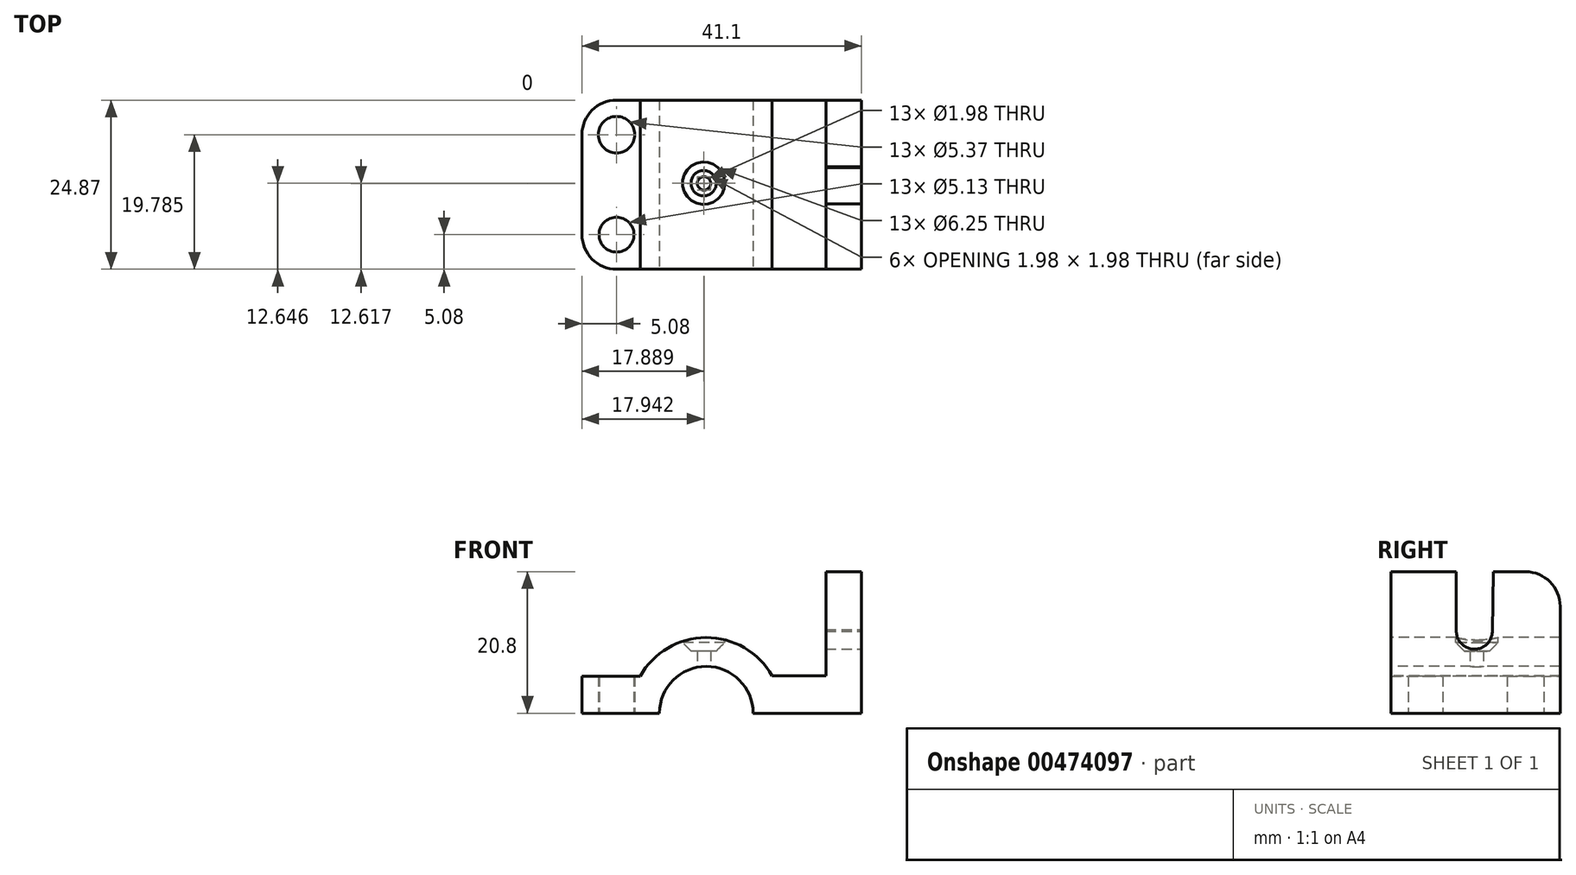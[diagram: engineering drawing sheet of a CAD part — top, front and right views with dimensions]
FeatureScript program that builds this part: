
annotation { "Feature Type Name" : "Feature", "Feature Type Description" : "" }
export const myFeature = defineFeature(function(context is Context, id is Id, definition is map)
    precondition{}
    {
        {
            var Q0;
            Q0=qCreatedBy(makeId("Top.planeOp"),FACE);
            var sketch = newSketch(context, id + "F0", { "sketchPlane" : qUnion([Q0])});
            skLineSegment(sketch, "E0.bottom", {"start": v(0, 0) * mm, "end": v(41.1, 0) * mm});
            skLineSegment(sketch, "E0.top", {"start": v(0, 24.87) * mm, "end": v(41.1, 24.87) * mm});
            skLineSegment(sketch, "E0.left", {"start": v(0, 0) * mm, "end": v(0, 24.87) * mm});
            skLineSegment(sketch, "E0.right", {"start": v(41.1, 0) * mm, "end": v(41.1, 24.87) * mm});
            skSolve(sketch);
        }
        {
            var Q0;
            Q0 = qSketchRegion(id + "F0", true);
            extrude(context, id + "F1", {"entities" : qUnion([Q0]), "depth" : 26.92 * mm});
        }
        {
            var Q0;
            Q0=qCreatedBy(makeId("Front.planeOp"),FACE);
            var sketch = newSketch(context, id + "F2", { "sketchPlane" : qUnion([Q0])});
            skArc(sketch, "E1", {"start": v(25.16, 0) * mm, "mid": v(18.28, 6.88) * mm, "end": v(11.4, 0) * mm});
            skArc(sketch, "E2", {"start": v(27.96, 5.5) * mm, "mid": v(18.23, 11.13) * mm, "end": v(8.55, 5.42) * mm});
            skLineSegment(sketch, "E3", {"start": v(0, 5.42) * mm, "end": v(8.55, 5.42) * mm});
            skLineSegment(sketch, "E4", {"start": v(27.96, 5.5) * mm, "end": v(35.86, 5.5) * mm});
            skLineSegment(sketch, "E5", {"start": v(35.86, 5.5) * mm, "end": v(35.86, 20.8) * mm});
            skLineSegment(sketch, "E6", {"start": v(35.86, 20.8) * mm, "end": v(43.18, 20.8) * mm});
            skLineSegment(sketch, "E7", {"start": v(43.18, 20.8) * mm, "end": v(42.24, 32.74) * mm});
            skLineSegment(sketch, "E8", {"start": v(42.24, 32.74) * mm, "end": v(-4.64, 32.74) * mm});
            skLineSegment(sketch, "E9", {"start": v(-4.64, 32.74) * mm, "end": v(0, 5.42) * mm});
            skLineSegment(sketch, "E10", {"start": v(11.4, 0) * mm, "end": v(25.16, 0) * mm});
            skPoint(sketch, "E11.start.orphan", {"position": v(7.14, 0) * mm});
            skSolve(sketch);
        }
        {
            var Q0;
            Q0 = qSketchRegion(id + "F2", true);
            extrude(context, id + "F3", {"entities" : qUnion([Q0]), "operationType" : NewBodyOperationType.REMOVE, "oppositeDirection" : true, "depth" : 33.02 * mm});
        }
        {
            var Q0;
            Q0=makeQuery(id+"F1.opExtrude","SWEPT_FACE",FACE,{"disambiguationData":[OSD([sQuery(id+"F0.wireOp",EDGE,"E0.right")])]});
            var sketch = newSketch(context, id + "F4", { "sketchPlane" : qUnion([Q0])});
            skArc(sketch, "E12", {"start": v(9.61, 12.3) * mm, "mid": v(12.14, 9.41) * mm, "end": v(14.9, 12.06) * mm});
            skLineSegment(sketch, "E13", {"start": v(9.61, 12.3) * mm, "end": v(9.61, 20.8) * mm});
            skLineSegment(sketch, "E14", {"start": v(9.61, 20.8) * mm, "end": v(15.04, 20.8) * mm});
            skLineSegment(sketch, "E15", {"start": v(14.9, 12.06) * mm, "end": v(15.04, 20.8) * mm});
            skSolve(sketch);
        }
        {
            var Q0;
            Q0 = qSketchRegion(id + "F4", true);
            extrude(context, id + "F5", {"entities" : qUnion([Q0]), "operationType" : NewBodyOperationType.REMOVE, "oppositeDirection" : true, "depth" : 9.9 * mm});
        }
        {
            var Q0;
            Q0=makeQuery(id+"F3.boolean.opBoolean","COPY",EDGE,{"derivedFrom":makeQuery(id+"F3.opExtrude","CAP_EDGE",EDGE,{"disambiguationData":[OSD([sQuery(id+"F2.wireOp",EDGE,"E6")])],"isStart":true})});
            var Q1;
            Q1=makeQuery(id+"F3.boolean.opBoolean","INTERSECT",EDGE,{"derivedFrom":[makeQuery(id+"F1.opExtrude","SWEPT_FACE",FACE,{"disambiguationData":[OSD([sQuery(id+"F0.wireOp",EDGE,"E0.top")])]}),makeQuery(id+"F3.opExtrude","SWEPT_FACE",FACE,{"disambiguationData":[OSD([sQuery(id+"F2.wireOp",EDGE,"E6")])]})]});
            var Q2;
            Q2=makeQuery(id+"F1.opExtrude","SWEPT_EDGE",EDGE,{"disambiguationData":[OSD([sQuery(id+"F0.wireOp",EDGE,"E0.top"),sQuery(id+"F0.wireOp",EDGE,"E0.left")])]});
            var Q3;
            Q3=makeQuery(id+"F1.opExtrude","SWEPT_EDGE",EDGE,{"disambiguationData":[OSD([sQuery(id+"F0.wireOp",EDGE,"E0.bottom"),sQuery(id+"F0.wireOp",EDGE,"E0.left")])]});
            fillet(context, id + "F6", {"entities" : qUnion([Q0, Q1, Q2, Q3]), "radius" : 5.08 * mm, "tangentPropagation" : true, "allowEdgeOverflow" : false});
        }
        {
            var Q0;
            {var subQ0=sQuery(id+"F0.wireOp",EDGE,"E0.bottom");var subQ1=sQuery(id+"F0.wireOp",EDGE,"E0.top");var subQ2=sQuery(id+"F0.wireOp",EDGE,"E0.left");Q0=makeQuery(id+"F3.boolean.opBoolean","SPLIT",FACE,{"disambiguationData":[TD([makeQuery(id+"F1.opExtrude","SWEPT_FACE",FACE,{"disambiguationData":[OSD([subQ2])]})])],"derivedFrom":makeQuery(id+"F1.opExtrude","CAP_FACE",FACE,{"disambiguationData":[OSD([subQ0,subQ1,subQ2,sQuery(id+"F0.wireOp",EDGE,"E0.right")])],"isStart":true})});}
            var sketch = newSketch(context, id + "F7", { "sketchPlane" : qUnion([Q0])});
            skCircle(sketch, "E16", {"center": v(5.08, -5.08) * mm, "radius": 2.57 * mm});
            skCircle(sketch, "E17", {"center": v(5.08, -19.79) * mm, "radius": 2.68 * mm});
            skCircle(sketch, "E18", {"center": v(17.94, -12.62) * mm, "radius": 0.99 * mm});
            skSolve(sketch);
        }
        {
            var Q0;
            Q0 = qSketchRegion(id + "F7", true);
            extrude(context, id + "F8", {"entities" : qUnion([Q0]), "operationType" : NewBodyOperationType.REMOVE, "oppositeDirection" : true, "depth" : 25.4 * mm});
        }
        {
            var Q0;
            Q0=qCreatedBy(makeId("Top.planeOp"),FACE);
            cPlane(context, id + "F9", {"entities" : qUnion([Q0]), "cplaneType" : CPlaneType.OFFSET, "offset" : 29.72 * mm, "width" : 152.4 * mm, "height" : 152.4 * mm});
        }
        {
            var Q0;
            Q0=qCreatedBy(id+"F9.planeOp",FACE);
            var sketch = newSketch(context, id + "F10", { "sketchPlane" : qUnion([Q0])});
            skCircle(sketch, "E19", {"center": v(17.89, 12.65) * mm, "radius": 3.12 * mm});
            skSolve(sketch);
        }
        {
            var Q0;
            Q0 = qSketchRegion(id + "F10", true);
            extrude(context, id + "F11", {"entities" : qUnion([Q0]), "operationType" : NewBodyOperationType.REMOVE, "oppositeDirection" : true, "depth" : 20.57 * mm});
        }
        {
            var Q0;
            Q0=makeQuery(id+"F11.boolean.opBoolean","COPY",EDGE,{"derivedFrom":makeQuery(id+"F11.opExtrude","CAP_EDGE",EDGE,{"disambiguationData":[OSD([sQuery(id+"F10.wireOp",EDGE,"E19")])],"isStart":false})});
            chamfer(context, id + "F12", {"entities" : qUnion([Q0]), "width" : 1.27 * mm, "tangentPropagation" : true});
        }
    });
